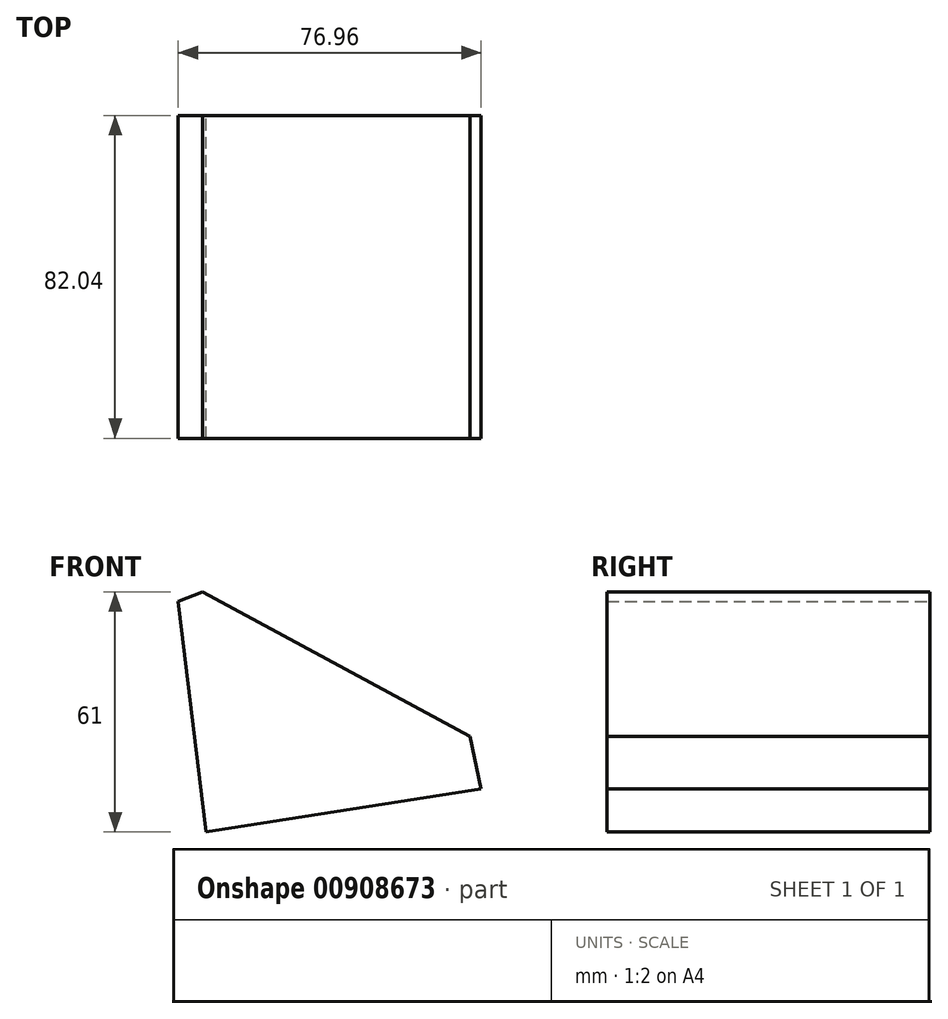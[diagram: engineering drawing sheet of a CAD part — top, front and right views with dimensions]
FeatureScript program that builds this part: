
annotation { "Feature Type Name" : "Feature", "Feature Type Description" : "" }
export const myFeature = defineFeature(function(context is Context, id is Id, definition is map)
    precondition{}
    {
        {
            var Q0;
            Q0=qCreatedBy(makeId("Front.planeOp"),FACE);
            var sketch = newSketch(context, id + "F0", { "sketchPlane" : qUnion([Q0])});
            skLineSegment(sketch, "E0", {"start": v(-44.74, 33.44) * mm, "end": v(16.95, 57.26) * mm});
            skLineSegment(sketch, "E1", {"start": v(16.95, 57.26) * mm, "end": v(32.22, -14.2) * mm});
            skLineSegment(sketch, "E2", {"start": v(32.22, -14.2) * mm, "end": v(-37.71, -25.2) * mm});
            skLineSegment(sketch, "E3", {"start": v(-37.71, -25.2) * mm, "end": v(-44.74, 33.44) * mm});
            skSolve(sketch);
        }
        {
            var Q0;
            Q0=makeQuery(id+"F0.imprint","IMPRINT",FACE,{"disambiguationData":[TD([[makeQuery(id+"F0.imprint","IMPRINT",EDGE,{"derivedFrom":sQuery(id+"F0.wireOp",EDGE,"E0")}),-1.0]])]});
            extrude(context, id + "F1", {"entities" : qUnion([Q0]), "depth" : 82.04 * mm, "offsetDistance" : 25.4 * mm});
        }
        {
            var Q0;
            Q0=makeQuery(id+"F1.opExtrude","SWEPT_EDGE",EDGE,{"disambiguationData":[OSD([sQuery(id+"F0.wireOp",EDGE,"E0"),sQuery(id+"F0.wireOp",EDGE,"E1")])]});
            chamfer(context, id + "F2", {"entities" : qUnion([Q0]), "width" : 50.8 * mm, "tangentPropagation" : true});
        }
    });
